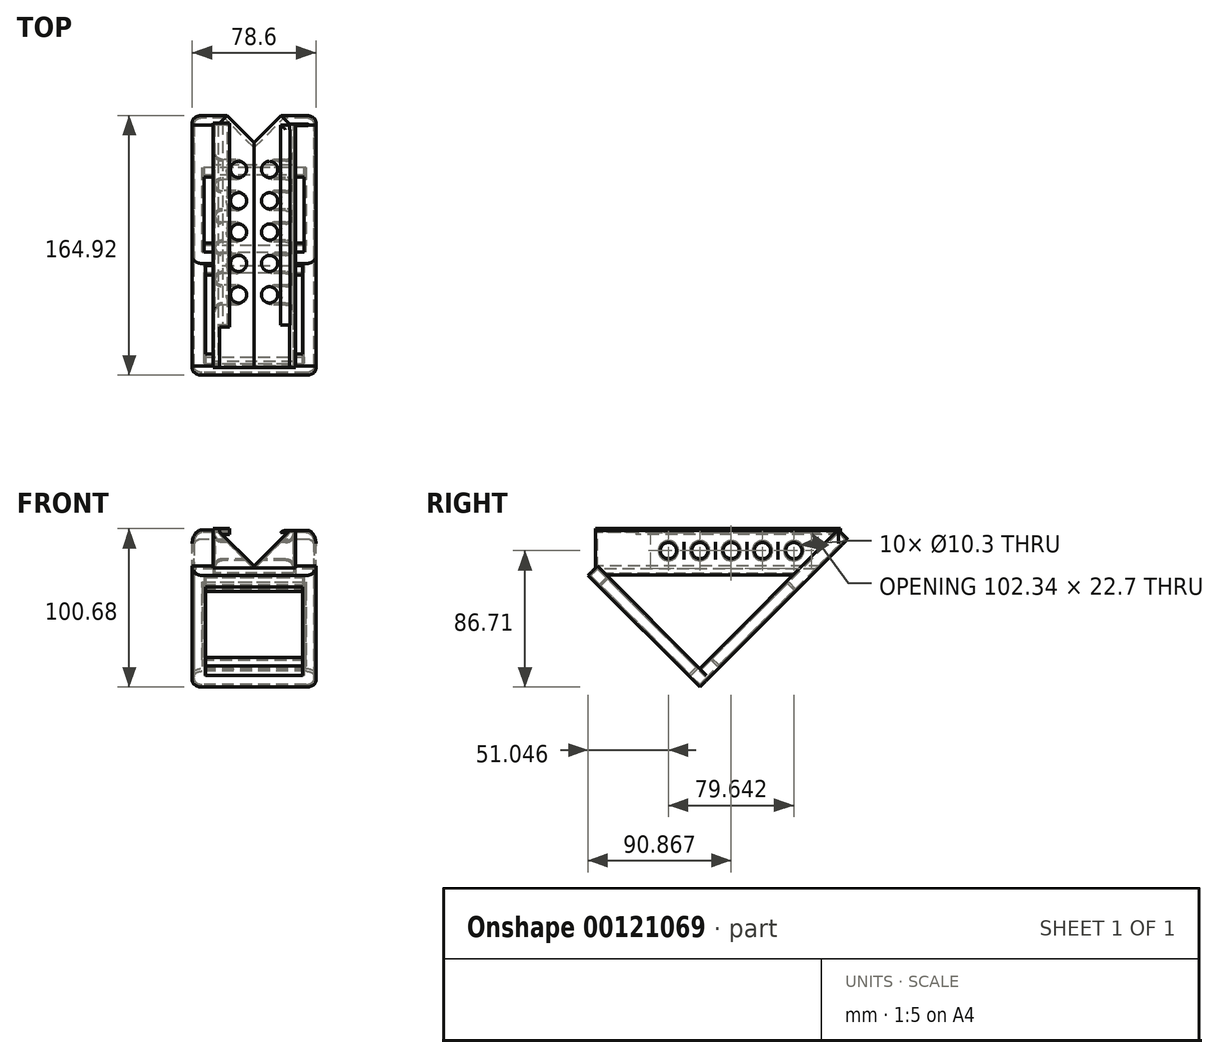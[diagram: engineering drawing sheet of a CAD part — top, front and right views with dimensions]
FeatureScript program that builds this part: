
annotation { "Feature Type Name" : "Feature", "Feature Type Description" : "" }
export const myFeature = defineFeature(function(context is Context, id is Id, definition is map)
    precondition{}
    {
        {
            var Q0;
            Q0=qCreatedBy(makeId("Front.planeOp"),FACE);
            var sketch = newSketch(context, id + "F0", { "sketchPlane" : qUnion([Q0])});
            skLineSegment(sketch, "E0", {"start": v(0, 0) * mm, "end": v(0, 23) * mm, "construction": true});
            skLineSegment(sketch, "E1", {"start": v(0, 0) * mm, "end": v(23, 23) * mm});
            skLineSegment(sketch, "E2", {"start": v(0, 0) * mm, "end": v(-23, 23) * mm});
            skLineSegment(sketch, "E3", {"start": v(-23, 23) * mm, "end": v(23, 23) * mm});
            skSolve(sketch);
        }
        {
            var Q0;
            Q0=qCreatedBy(makeId("Right.planeOp"),FACE);
            var sketch = newSketch(context, id + "F1", { "sketchPlane" : qUnion([Q0])});
            skPoint(sketch, "E4.0", {"position": v(0, 23) * mm});
            skLineSegment(sketch, "E5.0", {"start": v(0, 0) * mm, "end": v(0, 23) * mm, "construction": true});
            skLineSegment(sketch, "E6", {"start": v(-88.02, 23) * mm, "end": v(88.02, 23) * mm});
            skLineSegment(sketch, "E7", {"start": v(88.02, 23) * mm, "end": v(0, -65.02) * mm});
            skLineSegment(sketch, "E8", {"start": v(-65.02, 0) * mm, "end": v(65.02, 0) * mm, "construction": true});
            skLineSegment(sketch, "E9", {"start": v(-88.02, 23) * mm, "end": v(0, -65.02) * mm});
            skLineSegment(sketch, "E10", {"start": v(-88.02, 23) * mm, "end": v(-92.27, 18.76) * mm});
            skLineSegment(sketch, "E11", {"start": v(-92.27, 18.76) * mm, "end": v(0, -73.5) * mm});
            skLineSegment(sketch, "E12", {"start": v(0, -73.5) * mm, "end": v(92.27, 18.76) * mm});
            skLineSegment(sketch, "E13", {"start": v(92.27, 18.76) * mm, "end": v(88.02, 23) * mm});
            skLineSegment(sketch, "E14", {"start": v(-62.42, -2.6) * mm, "end": v(62.42, -2.6) * mm});
            skLineSegment(sketch, "E15", {"start": v(-65.02, 0) * mm, "end": v(-69.27, -4.24) * mm});
            skLineSegment(sketch, "E16", {"start": v(-65.02, 0) * mm, "end": v(-65.02, 23) * mm});
            skSolve(sketch);
        }
        {
            var Q0;
            {var subQ8=sQuery(id+"F1.wireOp",EDGE,"E12");Q0=makeQuery(id+"F1.imprint","IMPRINT",FACE,{"disambiguationData":[TD([[makeQuery(id+"F1.imprint","IMPRINT",EDGE,{"derivedFrom":subQ8}),1.0]])]});}
            extrude(context, id + "F2", {"entities" : qUnion([Q0]), "endBound" : BoundingType.SYMMETRIC, "depth" : 76.2 * mm});
        }
        {
            var Q0;
            {var subQ0=sQuery(id+"F1.wireOp",EDGE,"E14");Q0=makeQuery(id+"F1.imprint","IMPRINT",FACE,{"disambiguationData":[TD([[makeQuery(id+"F1.imprint","IMPRINT",EDGE,{"derivedFrom":subQ0}),1.0]])]});}
            extrude(context, id + "F3", {"entities" : qUnion([Q0]), "endBound" : BoundingType.SYMMETRIC, "depth" : 50 * mm});
        }
        {
            var Q0;
            Q0 = qSketchRegion(id + "F0", true);
            extrude(context, id + "F4", {"entities" : qUnion([Q0]), "operationType" : NewBodyOperationType.REMOVE, "endBound" : BoundingType.SYMMETRIC, "oppositeDirection" : true, "depth" : 200 * mm});
        }
        {
            var Q0;
            Q0=qCreatedBy(makeId("Top.planeOp"),FACE);
            var sketch = newSketch(context, id + "F5", { "sketchPlane" : qUnion([Q0])});
            skLineSegment(sketch, "E17.0", {"start": v(-22, 92.27) * mm, "end": v(-22, -62.42) * mm});
            skLineSegment(sketch, "E18.0", {"start": v(22, 92.27) * mm, "end": v(22, -62.42) * mm});
            skLineSegment(sketch, "E19", {"start": v(-22, -39.18) * mm, "end": v(-11.84, -39.18) * mm});
            skLineSegment(sketch, "E20", {"start": v(-11.84, -39.18) * mm, "end": v(-22, -50.42) * mm});
            skLineSegment(sketch, "E21", {"start": v(-22, -39.18) * mm, "end": v(22, -39.18) * mm, "construction": true});
            skPoint(sketch, "E22", {"position": v(0, -39.18) * mm});
            skLineSegment(sketch, "E23", {"start": v(22, -39.18) * mm, "end": v(11.84, -39.18) * mm});
            skLineSegment(sketch, "E24", {"start": v(11.84, -39.18) * mm, "end": v(22, -50.42) * mm});
            skPoint(sketch, "E25.0", {"position": v(0, 92.27) * mm});
            skLineSegment(sketch, "E26", {"start": v(-22, 92.27) * mm, "end": v(22, 92.27) * mm, "construction": true});
            skLineSegment(sketch, "E27.0", {"start": v(0, -65.02) * mm, "end": v(0, 65.02) * mm});
            skLineSegment(sketch, "E28.0", {"start": v(25, -62.42) * mm, "end": v(-25, -62.42) * mm});
            skSolve(sketch);
        }
        {
            var Q0;
            Q0=makeQuery(id+"F2.opExtrude","SWEPT_FACE",FACE,{"disambiguationData":[OSD([sQuery(id+"F1.wireOp",EDGE,"E12")])]});
            var sketch = newSketch(context, id + "F6", { "sketchPlane" : qUnion([Q0])});
            skLineSegment(sketch, "E29.bottom", {"start": v(38.1, -51.98) * mm, "end": v(22.56, -51.98) * mm, "construction": true});
            skLineSegment(sketch, "E29.top", {"start": v(38.1, -36.43) * mm, "end": v(22.56, -36.43) * mm});
            skLineSegment(sketch, "E29.left", {"start": v(38.1, -51.98) * mm, "end": v(38.1, -36.43) * mm});
            skLineSegment(sketch, "E29.right", {"start": v(22.56, -51.98) * mm, "end": v(22.56, -36.43) * mm});
            skLineSegment(sketch, "E30.bottom", {"start": v(-38.1, -51.98) * mm, "end": v(-22.55, -51.98) * mm, "construction": true});
            skLineSegment(sketch, "E30.top", {"start": v(-38.1, -36.43) * mm, "end": v(-22.55, -36.43) * mm});
            skLineSegment(sketch, "E30.left", {"start": v(-38.1, -51.98) * mm, "end": v(-38.1, -36.43) * mm, "construction": true});
            skLineSegment(sketch, "E30.right", {"start": v(-22.55, -51.98) * mm, "end": v(-22.55, -36.43) * mm});
            skLineSegment(sketch, "E31.bottom", {"start": v(22.56, 78.5) * mm, "end": v(38.1, 78.5) * mm, "construction": true});
            skLineSegment(sketch, "E31.top", {"start": v(22.56, 62.96) * mm, "end": v(38.1, 62.96) * mm});
            skLineSegment(sketch, "E31.left", {"start": v(22.56, 78.5) * mm, "end": v(22.56, 62.96) * mm});
            skLineSegment(sketch, "E31.right", {"start": v(38.1, 78.5) * mm, "end": v(38.1, 62.96) * mm, "construction": true});
            skCircle(sketch, "E32", {"center": v(-30.32, -44.2) * mm, "radius": 7 * mm});
            skCircle(sketch, "E33", {"center": v(30.33, -44.2) * mm, "radius": 7 * mm});
            skPoint(sketch, "E33.centerSnap0", {"position": v(30.33, -51.98) * mm});
            skCircle(sketch, "E34", {"center": v(30.33, 70.73) * mm, "radius": 7 * mm});
            skLineSegment(sketch, "E35", {"start": v(-30.32, -51.98) * mm, "end": v(-30.32, -36.43) * mm, "construction": true});
            skLineSegment(sketch, "E36", {"start": v(30.33, -51.98) * mm, "end": v(30.33, -36.43) * mm, "construction": true});
            skLineSegment(sketch, "E37", {"start": v(30.33, 78.5) * mm, "end": v(30.33, 62.96) * mm, "construction": true});
            skLineSegment(sketch, "E38.0.0", {"start": v(18.76, 78.5) * mm, "end": v(0, 51.98) * mm});
            skLineSegment(sketch, "E38.0.1", {"start": v(0, 51.98) * mm, "end": v(-18.76, 78.5) * mm});
            skLineSegment(sketch, "E38.0.2", {"start": v(-18.76, 78.5) * mm, "end": v(-38.1, 78.5) * mm});
            skLineSegment(sketch, "E38.0.3", {"start": v(-38.1, 78.5) * mm, "end": v(-38.1, -51.98) * mm});
            skLineSegment(sketch, "E38.0.4", {"start": v(-38.1, -51.98) * mm, "end": v(38.1, -51.98) * mm});
            skLineSegment(sketch, "E38.0.5", {"start": v(38.1, -51.98) * mm, "end": v(38.1, 78.5) * mm});
            skLineSegment(sketch, "E38.0.6", {"start": v(38.1, 78.5) * mm, "end": v(18.76, 78.5) * mm});
            skPoint(sketch, "E39.0", {"position": v(0, 78.5) * mm});
            skLineSegment(sketch, "E40.bottom", {"start": v(-38.1, 78.5) * mm, "end": v(-22.56, 78.5) * mm, "construction": true});
            skLineSegment(sketch, "E40.top", {"start": v(-38.1, 62.96) * mm, "end": v(-22.56, 62.96) * mm});
            skLineSegment(sketch, "E40.left", {"start": v(-38.1, 78.5) * mm, "end": v(-38.1, 62.96) * mm, "construction": true});
            skLineSegment(sketch, "E40.right", {"start": v(-22.56, 78.5) * mm, "end": v(-22.56, 62.96) * mm});
            skCircle(sketch, "E41", {"center": v(-30.33, 70.73) * mm, "radius": 7 * mm});
            skLineSegment(sketch, "E42", {"start": v(-30.33, 78.5) * mm, "end": v(-30.33, 62.96) * mm, "construction": true});
            skSolve(sketch);
        }
        {
            var Q0;
            {var subQ2=sQuery(id+"F1.wireOp",EDGE,"E6");Q0=makeQuery(id+"F4.boolean.opBoolean","SPLIT",FACE,{"disambiguationData":[TD([makeQuery(id+"F4.opExtrude","SWEPT_FACE",FACE,{"disambiguationData":[OSD([sQuery(id+"F0.wireOp",EDGE,"E1")])]})])],"derivedFrom":makeQuery(id+"F3.opExtrude","SWEPT_FACE",FACE,{"disambiguationData":[OSD([subQ2])]})});}
            var sketch = newSketch(context, id + "F7", { "sketchPlane" : qUnion([Q0])});
            skLineSegment(sketch, "E43.0.0", {"start": v(22, -50.42) * mm, "end": v(22, -39.18) * mm});
            skLineSegment(sketch, "E43.0.1", {"start": v(22, -39.18) * mm, "end": v(11.84, -39.18) * mm});
            skLineSegment(sketch, "E43.0.2", {"start": v(11.84, -39.18) * mm, "end": v(22, -50.42) * mm});
            skLineSegment(sketch, "E44.0.0", {"start": v(-11.84, -39.18) * mm, "end": v(-22, -39.18) * mm});
            skLineSegment(sketch, "E44.0.1", {"start": v(-22, -39.18) * mm, "end": v(-22, -50.42) * mm});
            skLineSegment(sketch, "E44.0.2", {"start": v(-22, -50.42) * mm, "end": v(-11.84, -39.18) * mm});
            skLineSegment(sketch, "E45.0.5", {"start": v(25, -39.18) * mm, "end": v(25, 88.02) * mm});
            skLineSegment(sketch, "E46.0.2", {"start": v(-25, 88.02) * mm, "end": v(-25, -39.18) * mm});
            skLineSegment(sketch, "E47.bottom", {"start": v(25, -39.18) * mm, "end": v(16.92, -39.18) * mm});
            skLineSegment(sketch, "E47.top", {"start": v(25, 88.02) * mm, "end": v(16.92, 88.02) * mm});
            skLineSegment(sketch, "E47.right", {"start": v(16.92, -39.18) * mm, "end": v(16.92, 88.02) * mm});
            skPoint(sketch, "E48.oppositeSnap0", {"position": v(-16.92, -39.18) * mm});
            skLineSegment(sketch, "E48.bottom", {"start": v(-25, -39.18) * mm, "end": v(-16.92, -39.18) * mm});
            skLineSegment(sketch, "E48.top", {"start": v(-25, 88.02) * mm, "end": v(-16.92, 88.02) * mm});
            skLineSegment(sketch, "E48.left", {"start": v(-25, -39.18) * mm, "end": v(-25, 88.02) * mm});
            skLineSegment(sketch, "E48.right", {"start": v(-16.92, -39.18) * mm, "end": v(-16.92, 88.02) * mm});
            skPoint(sketch, "E49.0", {"position": v(0, 65.02) * mm});
            skPoint(sketch, "E50.0", {"position": v(-25, 88.02) * mm});
            skPoint(sketch, "E51.0", {"position": v(25, 88.02) * mm});
            skSolve(sketch);
        }
        {
            var Q0;
            Q0=qCreatedBy(makeId("Right.planeOp"),FACE);
            var sketch = newSketch(context, id + "F8", { "sketchPlane" : qUnion([Q0])});
            skLineSegment(sketch, "E52.0.1", {"start": v(0, 0) * mm, "end": v(0, 23) * mm, "construction": true});
            skLineSegment(sketch, "E52.0.2", {"start": v(0, 23) * mm, "end": v(-88.02, 23) * mm});
            skLineSegment(sketch, "E53.0.3", {"start": v(88.02, 23) * mm, "end": v(0, 23) * mm});
            skPoint(sketch, "E54.0", {"position": v(0, 23) * mm});
            skLineSegment(sketch, "E55", {"start": v(19.91, 0) * mm, "end": v(19.91, 23) * mm, "construction": true});
            skLineSegment(sketch, "E56", {"start": v(39.81, 0) * mm, "end": v(39.81, 23) * mm, "construction": true});
            skPoint(sketch, "E57", {"position": v(0, 11.5) * mm});
            skPoint(sketch, "E58", {"position": v(19.91, 11.5) * mm});
            skPoint(sketch, "E59", {"position": v(39.81, 11.5) * mm});
            skCircle(sketch, "E60", {"center": v(0, 11.5) * mm, "radius": 6.35 * mm});
            skCircle(sketch, "E61", {"center": v(19.91, 11.5) * mm, "radius": 6.35 * mm});
            skCircle(sketch, "E62", {"center": v(39.81, 11.5) * mm, "radius": 6.35 * mm});
            skLineSegment(sketch, "E63", {"start": v(-19.91, 0) * mm, "end": v(-19.91, 23) * mm, "construction": true});
            skPoint(sketch, "E64", {"position": v(-19.91, 11.5) * mm});
            skCircle(sketch, "E65", {"center": v(-19.91, 11.5) * mm, "radius": 6.35 * mm});
            skLineSegment(sketch, "E66", {"start": v(59.73, 0) * mm, "end": v(59.73, 23) * mm, "construction": true});
            skPoint(sketch, "E67", {"position": v(59.73, 11.5) * mm});
            skCircle(sketch, "E68", {"center": v(59.73, 11.5) * mm, "radius": 6.35 * mm});
            skPoint(sketch, "E69.0", {"position": v(-88.02, 23) * mm});
            skPoint(sketch, "E70.0", {"position": v(88.02, 23) * mm});
            skLineSegment(sketch, "E71.0", {"start": v(-65.02, 0) * mm, "end": v(65.02, 0) * mm});
            skSolve(sketch);
        }
        {
            var Q0;
            Q0=makeQuery(id+"F8.imprint","IMPRINT",FACE,{"disambiguationData":[TD([[makeQuery(id+"F8.imprint","IMPRINT",EDGE,{"derivedFrom":sQuery(id+"F8.wireOp",EDGE,"E65")}),1.0]])]});
            var Q1;
            Q1=makeQuery(id+"F8.imprint","IMPRINT",FACE,{"disambiguationData":[TD([[makeQuery(id+"F8.imprint","IMPRINT",EDGE,{"derivedFrom":sQuery(id+"F8.wireOp",EDGE,"E60")}),1.0]])]});
            var Q2;
            Q2=makeQuery(id+"F8.imprint","IMPRINT",FACE,{"disambiguationData":[TD([[makeQuery(id+"F8.imprint","IMPRINT",EDGE,{"derivedFrom":sQuery(id+"F8.wireOp",EDGE,"E61")}),1.0]])]});
            var Q3;
            Q3=makeQuery(id+"F8.imprint","IMPRINT",FACE,{"disambiguationData":[TD([[makeQuery(id+"F8.imprint","IMPRINT",EDGE,{"derivedFrom":sQuery(id+"F8.wireOp",EDGE,"E62")}),1.0]])]});
            var Q4;
            Q4=makeQuery(id+"F8.imprint","IMPRINT",FACE,{"disambiguationData":[TD([[makeQuery(id+"F8.imprint","IMPRINT",EDGE,{"derivedFrom":sQuery(id+"F8.wireOp",EDGE,"E68")}),1.0]])]});
            extrude(context, id + "F9", {"entities" : qUnion([Q0, Q1, Q2, Q3, Q4]), "operationType" : NewBodyOperationType.REMOVE, "endBound" : BoundingType.SYMMETRIC, "depth" : 177.8 * mm});
        }
        {
            var Q0;
            {var subQ4=sQuery(id+"F7.wireOp",EDGE,"E45.0.5");Q0=makeQuery(id+"F7.imprint","IMPRINT",FACE,{"disambiguationData":[TD([[makeQuery(id+"F7.imprint","IMPRINT",EDGE,{"derivedFrom":subQ4}),1.0]])]});}
            var Q1;
            {var subQ3=sQuery(id+"F7.wireOp",EDGE,"E47.right");Q1=makeQuery(id+"F7.imprint","IMPRINT",FACE,{"disambiguationData":[TD([[makeQuery(id+"F7.imprint","IMPRINT",EDGE,{"derivedFrom":subQ3}),-1.0]])]});}
            var Q2;
            Q2=makeQuery(id+"F7.imprint","IMPRINT",FACE,{"disambiguationData":[TD([[makeQuery(id+"F7.imprint","IMPRINT",EDGE,{"derivedFrom":sQuery(id+"F7.wireOp",EDGE,"E48.top")}),-1.0]])]});
            var Q3;
            {var subQ0=sQuery(id+"F7.wireOp",EDGE,"E43.0.0");Q3=makeQuery(id+"F7.imprint","IMPRINT",FACE,{"disambiguationData":[TD([[makeQuery(id+"F7.imprint","IMPRINT",EDGE,{"derivedFrom":subQ0}),-1.0]])]});}
            var Q4;
            {var subQ2=sQuery(id+"F1.wireOp",EDGE,"E6");Q4=makeQuery(id+"F4.boolean.opBoolean","SPLIT",FACE,{"disambiguationData":[TD([makeQuery(id+"F4.opExtrude","SWEPT_FACE",FACE,{"disambiguationData":[OSD([sQuery(id+"F0.wireOp",EDGE,"E2")])]})])],"derivedFrom":makeQuery(id+"F3.opExtrude","SWEPT_FACE",FACE,{"disambiguationData":[OSD([subQ2])]})});}
            extrude(context, id + "F10", {"entities" : qUnion([Q0, Q1, Q2, Q3, Q4]), "operationType" : NewBodyOperationType.ADD, "depth" : 1.27 * mm});
        }
        {
            var Q0;
            {var subQ0=sQuery(id+"F6.wireOp",EDGE,"E38.0.4");Q0=makeQuery(id+"FcCoG44jGWUjaJj_4.boolean.opBoolean","MERGE",FACE,{"derivedFrom":[makeQuery(id+"F2.opExtrude","SWEPT_FACE",FACE,{"disambiguationData":[OSD([sQuery(id+"F1.wireOp",EDGE,"E11")])]}),makeQuery(id+"FcCoG44jGWUjaJj_4.opExtrude","SWEPT_FACE",FACE,{"disambiguationData":[OSD([subQ0]),TDD([makeQuery(id+"F6.imprint","IMPRINT",EDGE,{"disambiguationData":[TD([[makeQuery(id+"F6.imprint","INTERSECT",VERTEX,{"derivedFrom":[sQuery(id+"F6.wireOp",EDGE,"E38.0.3"),subQ0]}),-1.0]])],"derivedFrom":subQ0})])]}),makeQuery(id+"FcCoG44jGWUjaJj_4.opExtrude","SWEPT_FACE",FACE,{"disambiguationData":[OSD([subQ0]),TDD([makeQuery(id+"F6.imprint","IMPRINT",EDGE,{"disambiguationData":[TD([[makeQuery(id+"F6.imprint","INTERSECT",VERTEX,{"derivedFrom":[subQ0,sQuery(id+"F6.wireOp",EDGE,"E38.0.5")]}),1.0]])],"derivedFrom":subQ0})])]})]});}
            var sketch = newSketch(context, id + "F11", { "sketchPlane" : qUnion([Q0])});
            skLineSegment(sketch, "E72.bottom", {"start": v(-31.85, 37.98) * mm, "end": v(31.85, 37.98) * mm});
            skLineSegment(sketch, "E72.top", {"start": v(-31.85, -43.88) * mm, "end": v(31.85, -43.88) * mm});
            skLineSegment(sketch, "E72.left", {"start": v(-31.85, 37.98) * mm, "end": v(-31.85, -43.88) * mm});
            skLineSegment(sketch, "E72.right", {"start": v(31.85, 37.98) * mm, "end": v(31.85, -43.88) * mm});
            skPoint(sketch, "E73.0", {"position": v(-38.1, 45.98) * mm});
            skPoint(sketch, "E74.0", {"position": v(38.1, -45.98) * mm});
            skLineSegment(sketch, "E75.0", {"start": v(22.55, -51.98) * mm, "end": v(-22.56, -51.98) * mm});
            skPoint(sketch, "E76.0", {"position": v(0, 45.98) * mm});
            skSolve(sketch);
        }
        {
            var Q0;
            Q0=makeQuery(id+"F11.imprint","IMPRINT",FACE,{"disambiguationData":[TD([[makeQuery(id+"F11.imprint","IMPRINT",EDGE,{"derivedFrom":sQuery(id+"F11.wireOp",EDGE,"E72.bottom")}),-1.0]])]});
            var Q1;
            Q1=makeQuery(id+"F2.opExtrude","SWEPT_FACE",FACE,{"disambiguationData":[OSD([sQuery(id+"F1.wireOp",EDGE,"E9")])]});
            extrude(context, id + "F12", {"entities" : qUnion([Q0]), "operationType" : NewBodyOperationType.REMOVE, "endBound" : BoundingType.UP_TO_SURFACE, "oppositeDirection" : true, "endBoundEntityFace" : qUnion([Q1]), "depth" : 25.4 * mm});
        }
        {
            var Q0;
            Q0=makeQuery(id+"FcCoG44jGWUjaJj_4.opExtrude","SWEPT_EDGE",EDGE,{"disambiguationData":[OSD([sQuery(id+"F6.wireOp",EDGE,"E31.top"),sQuery(id+"F6.wireOp",EDGE,"E38.0.5")])]});
            var Q1;
            Q1=makeQuery(id+"F2.opExtrude","CAP_EDGE",EDGE,{"disambiguationData":[OSD([sQuery(id+"F1.wireOp",EDGE,"E7")])],"isStart":true});
            var Q2;
            Q2=makeQuery(id+"F2.opExtrude","CAP_EDGE",EDGE,{"disambiguationData":[OSD([sQuery(id+"F1.wireOp",EDGE,"E7")])],"isStart":false});
            var Q3;
            Q3=makeQuery(id+"FcCoG44jGWUjaJj_4.boolean.opBoolean","MERGE",EDGE,{"derivedFrom":[makeQuery(id+"F2.opExtrude","CAP_EDGE",EDGE,{"disambiguationData":[OSD([sQuery(id+"F1.wireOp",EDGE,"E11")])],"isStart":false}),makeQuery(id+"FcCoG44jGWUjaJj_4.opExtrude","SWEPT_EDGE",EDGE,{"disambiguationData":[OSD([sQuery(id+"F6.wireOp",EDGE,"E38.0.3"),sQuery(id+"F6.wireOp",EDGE,"E38.0.4")])]})]});
            var Q4;
            Q4=makeQuery(id+"FcCoG44jGWUjaJj_4.boolean.opBoolean","MERGE",EDGE,{"derivedFrom":[makeQuery(id+"F2.opExtrude","CAP_EDGE",EDGE,{"disambiguationData":[OSD([sQuery(id+"F1.wireOp",EDGE,"E11")])],"isStart":true}),makeQuery(id+"FcCoG44jGWUjaJj_4.opExtrude","SWEPT_EDGE",EDGE,{"disambiguationData":[OSD([sQuery(id+"F6.wireOp",EDGE,"E38.0.4"),sQuery(id+"F6.wireOp",EDGE,"E38.0.5")])]})]});
            var Q5;
            Q5=makeQuery(id+"FcCoG44jGWUjaJj_4.opExtrude","SWEPT_EDGE",EDGE,{"disambiguationData":[OSD([sQuery(id+"F6.wireOp",EDGE,"E29.right"),sQuery(id+"F6.wireOp",EDGE,"E38.0.4")])]});
            var Q6;
            Q6=makeQuery(id+"FcCoG44jGWUjaJj_4.opExtrude","SWEPT_EDGE",EDGE,{"disambiguationData":[OSD([sQuery(id+"F6.wireOp",EDGE,"E30.right"),sQuery(id+"F6.wireOp",EDGE,"E38.0.4")])]});
            var Q7;
            Q7=makeQuery(id+"FcCoG44jGWUjaJj_4.opExtrude","SWEPT_EDGE",EDGE,{"disambiguationData":[OSD([sQuery(id+"F6.wireOp",EDGE,"E30.top"),sQuery(id+"F6.wireOp",EDGE,"E30.right")])]});
            var Q8;
            Q8=makeQuery(id+"FcCoG44jGWUjaJj_4.opExtrude","SWEPT_EDGE",EDGE,{"disambiguationData":[OSD([sQuery(id+"F6.wireOp",EDGE,"E30.top"),sQuery(id+"F6.wireOp",EDGE,"E38.0.3")])]});
            var Q9;
            Q9=makeQuery(id+"FcCoG44jGWUjaJj_4.opExtrude","SWEPT_EDGE",EDGE,{"disambiguationData":[OSD([sQuery(id+"F6.wireOp",EDGE,"E38.0.3"),sQuery(id+"F6.wireOp",EDGE,"E40.top")])]});
            var Q10;
            Q10=makeQuery(id+"FcCoG44jGWUjaJj_4.opExtrude","SWEPT_EDGE",EDGE,{"disambiguationData":[OSD([sQuery(id+"F6.wireOp",EDGE,"E40.top"),sQuery(id+"F6.wireOp",EDGE,"E40.right")])]});
            var Q11;
            Q11=makeQuery(id+"FcCoG44jGWUjaJj_4.boolean.opBoolean","MERGE",EDGE,{"derivedFrom":[makeQuery(id+"F2.opExtrude","CAP_EDGE",EDGE,{"disambiguationData":[OSD([sQuery(id+"F1.wireOp",EDGE,"E13")])],"isStart":false}),makeQuery(id+"FcCoG44jGWUjaJj_4.opExtrude","SWEPT_EDGE",EDGE,{"disambiguationData":[OSD([sQuery(id+"F6.wireOp",EDGE,"E38.0.2"),sQuery(id+"F6.wireOp",EDGE,"E38.0.3")])]})]});
            var Q12;
            Q12=makeQuery(id+"FcCoG44jGWUjaJj_4.opExtrude","SWEPT_EDGE",EDGE,{"disambiguationData":[OSD([sQuery(id+"F6.wireOp",EDGE,"E38.0.2"),sQuery(id+"F6.wireOp",EDGE,"E40.right")])]});
            var Q13;
            Q13=makeQuery(id+"FcCoG44jGWUjaJj_4.opExtrude","SWEPT_EDGE",EDGE,{"disambiguationData":[OSD([sQuery(id+"F6.wireOp",EDGE,"E31.left"),sQuery(id+"F6.wireOp",EDGE,"E38.0.6")])]});
            var Q14;
            Q14=makeQuery(id+"FcCoG44jGWUjaJj_4.boolean.opBoolean","MERGE",EDGE,{"derivedFrom":[makeQuery(id+"F2.opExtrude","CAP_EDGE",EDGE,{"disambiguationData":[OSD([sQuery(id+"F1.wireOp",EDGE,"E13")])],"isStart":true}),makeQuery(id+"FcCoG44jGWUjaJj_4.opExtrude","SWEPT_EDGE",EDGE,{"disambiguationData":[OSD([sQuery(id+"F6.wireOp",EDGE,"E38.0.5"),sQuery(id+"F6.wireOp",EDGE,"E38.0.6")])]})]});
            var Q15;
            Q15=makeQuery(id+"FcCoG44jGWUjaJj_4.opExtrude","SWEPT_EDGE",EDGE,{"disambiguationData":[OSD([sQuery(id+"F6.wireOp",EDGE,"E31.top"),sQuery(id+"F6.wireOp",EDGE,"E31.left")])]});
            var Q16;
            Q16=makeQuery(id+"FcCoG44jGWUjaJj_4.opExtrude","SWEPT_EDGE",EDGE,{"disambiguationData":[OSD([sQuery(id+"F6.wireOp",EDGE,"E29.top"),sQuery(id+"F6.wireOp",EDGE,"E29.right")])]});
            var Q17;
            Q17=makeQuery(id+"FcCoG44jGWUjaJj_4.opExtrude","SWEPT_EDGE",EDGE,{"disambiguationData":[OSD([sQuery(id+"F6.wireOp",EDGE,"E29.top"),sQuery(id+"F6.wireOp",EDGE,"E38.0.5")])]});
            var Q18;
            Q18=makeQuery(id+"F9.boolean.opBoolean","INTERSECT",EDGE,{"derivedFrom":[makeQuery(id+"F3.opExtrude","CAP_FACE",FACE,{"disambiguationData":[OSD([sQuery(id+"F1.wireOp",EDGE,"E6"),sQuery(id+"F1.wireOp",EDGE,"E7"),sQuery(id+"F1.wireOp",EDGE,"E9"),sQuery(id+"F1.wireOp",EDGE,"E14"),sQuery(id+"F1.wireOp",EDGE,"E16")])],"isStart":false}),makeQuery(id+"F9.opExtrude","SWEPT_FACE",FACE,{"disambiguationData":[OSD([sQuery(id+"F8.wireOp",EDGE,"E65")])]})]});
            var Q19;
            Q19=makeQuery(id+"F9.boolean.opBoolean","INTERSECT",EDGE,{"derivedFrom":[makeQuery(id+"F3.opExtrude","CAP_FACE",FACE,{"disambiguationData":[OSD([sQuery(id+"F1.wireOp",EDGE,"E6"),sQuery(id+"F1.wireOp",EDGE,"E7"),sQuery(id+"F1.wireOp",EDGE,"E9"),sQuery(id+"F1.wireOp",EDGE,"E14"),sQuery(id+"F1.wireOp",EDGE,"E16")])],"isStart":false}),makeQuery(id+"F9.opExtrude","SWEPT_FACE",FACE,{"disambiguationData":[OSD([sQuery(id+"F8.wireOp",EDGE,"E60")])]})]});
            var Q20;
            Q20=makeQuery(id+"F9.boolean.opBoolean","INTERSECT",EDGE,{"derivedFrom":[makeQuery(id+"F3.opExtrude","CAP_FACE",FACE,{"disambiguationData":[OSD([sQuery(id+"F1.wireOp",EDGE,"E6"),sQuery(id+"F1.wireOp",EDGE,"E7"),sQuery(id+"F1.wireOp",EDGE,"E9"),sQuery(id+"F1.wireOp",EDGE,"E14"),sQuery(id+"F1.wireOp",EDGE,"E16")])],"isStart":false}),makeQuery(id+"F9.opExtrude","SWEPT_FACE",FACE,{"disambiguationData":[OSD([sQuery(id+"F8.wireOp",EDGE,"E61")])]})]});
            var Q21;
            Q21=makeQuery(id+"F9.boolean.opBoolean","INTERSECT",EDGE,{"derivedFrom":[makeQuery(id+"F3.opExtrude","CAP_FACE",FACE,{"disambiguationData":[OSD([sQuery(id+"F1.wireOp",EDGE,"E6"),sQuery(id+"F1.wireOp",EDGE,"E7"),sQuery(id+"F1.wireOp",EDGE,"E9"),sQuery(id+"F1.wireOp",EDGE,"E14"),sQuery(id+"F1.wireOp",EDGE,"E16")])],"isStart":false}),makeQuery(id+"F9.opExtrude","SWEPT_FACE",FACE,{"disambiguationData":[OSD([sQuery(id+"F8.wireOp",EDGE,"E62")])]})]});
            var Q22;
            Q22=makeQuery(id+"F9.boolean.opBoolean","INTERSECT",EDGE,{"derivedFrom":[makeQuery(id+"F3.opExtrude","CAP_FACE",FACE,{"disambiguationData":[OSD([sQuery(id+"F1.wireOp",EDGE,"E6"),sQuery(id+"F1.wireOp",EDGE,"E7"),sQuery(id+"F1.wireOp",EDGE,"E9"),sQuery(id+"F1.wireOp",EDGE,"E14"),sQuery(id+"F1.wireOp",EDGE,"E16")])],"isStart":false}),makeQuery(id+"F9.opExtrude","SWEPT_FACE",FACE,{"disambiguationData":[OSD([sQuery(id+"F8.wireOp",EDGE,"E68")])]})]});
            var Q23;
            Q23=makeQuery(id+"F9.boolean.opBoolean","INTERSECT",EDGE,{"derivedFrom":[makeQuery(id+"F3.opExtrude","CAP_FACE",FACE,{"disambiguationData":[OSD([sQuery(id+"F1.wireOp",EDGE,"E6"),sQuery(id+"F1.wireOp",EDGE,"E7"),sQuery(id+"F1.wireOp",EDGE,"E9"),sQuery(id+"F1.wireOp",EDGE,"E14"),sQuery(id+"F1.wireOp",EDGE,"E16")])],"isStart":true}),makeQuery(id+"F9.opExtrude","SWEPT_FACE",FACE,{"disambiguationData":[OSD([sQuery(id+"F8.wireOp",EDGE,"E65")])]})]});
            var Q24;
            Q24=makeQuery(id+"F9.boolean.opBoolean","INTERSECT",EDGE,{"derivedFrom":[makeQuery(id+"F3.opExtrude","CAP_FACE",FACE,{"disambiguationData":[OSD([sQuery(id+"F1.wireOp",EDGE,"E6"),sQuery(id+"F1.wireOp",EDGE,"E7"),sQuery(id+"F1.wireOp",EDGE,"E9"),sQuery(id+"F1.wireOp",EDGE,"E14"),sQuery(id+"F1.wireOp",EDGE,"E16")])],"isStart":true}),makeQuery(id+"F9.opExtrude","SWEPT_FACE",FACE,{"disambiguationData":[OSD([sQuery(id+"F8.wireOp",EDGE,"E60")])]})]});
            var Q25;
            Q25=makeQuery(id+"F9.boolean.opBoolean","INTERSECT",EDGE,{"derivedFrom":[makeQuery(id+"F3.opExtrude","CAP_FACE",FACE,{"disambiguationData":[OSD([sQuery(id+"F1.wireOp",EDGE,"E6"),sQuery(id+"F1.wireOp",EDGE,"E7"),sQuery(id+"F1.wireOp",EDGE,"E9"),sQuery(id+"F1.wireOp",EDGE,"E14"),sQuery(id+"F1.wireOp",EDGE,"E16")])],"isStart":true}),makeQuery(id+"F9.opExtrude","SWEPT_FACE",FACE,{"disambiguationData":[OSD([sQuery(id+"F8.wireOp",EDGE,"E61")])]})]});
            var Q26;
            Q26=makeQuery(id+"F9.boolean.opBoolean","INTERSECT",EDGE,{"derivedFrom":[makeQuery(id+"F3.opExtrude","CAP_FACE",FACE,{"disambiguationData":[OSD([sQuery(id+"F1.wireOp",EDGE,"E6"),sQuery(id+"F1.wireOp",EDGE,"E7"),sQuery(id+"F1.wireOp",EDGE,"E9"),sQuery(id+"F1.wireOp",EDGE,"E14"),sQuery(id+"F1.wireOp",EDGE,"E16")])],"isStart":true}),makeQuery(id+"F9.opExtrude","SWEPT_FACE",FACE,{"disambiguationData":[OSD([sQuery(id+"F8.wireOp",EDGE,"E62")])]})]});
            var Q27;
            Q27=makeQuery(id+"F9.boolean.opBoolean","INTERSECT",EDGE,{"derivedFrom":[makeQuery(id+"F3.opExtrude","CAP_FACE",FACE,{"disambiguationData":[OSD([sQuery(id+"F1.wireOp",EDGE,"E6"),sQuery(id+"F1.wireOp",EDGE,"E7"),sQuery(id+"F1.wireOp",EDGE,"E9"),sQuery(id+"F1.wireOp",EDGE,"E14"),sQuery(id+"F1.wireOp",EDGE,"E16")])],"isStart":true}),makeQuery(id+"F9.opExtrude","SWEPT_FACE",FACE,{"disambiguationData":[OSD([sQuery(id+"F8.wireOp",EDGE,"E68")])]})]});
            fillet(context, id + "F13", {"entities" : qUnion([Q0, Q1, Q2, Q3, Q4, Q5, Q6, Q7, Q8, Q9, Q10, Q11, Q12, Q13, Q14, Q15, Q16, Q17, Q18, Q19, Q20, Q21, Q22, Q23, Q24, Q25, Q26, Q27]), "radius" : 5 * mm, "tangentPropagation" : true, "allowEdgeOverflow" : false});
        }
        {
            var Q0;
            Q0=makeQuery(id+"F10.opExtrude","CAP_EDGE",EDGE,{"disambiguationData":[OSD([sQuery(id+"F1.wireOp",EDGE,"E6")])],"isStart":false});
            var Q1;
            Q1=makeQuery(id+"F10.opExtrude","CAP_EDGE",EDGE,{"disambiguationData":[OSD([sQuery(id+"F1.wireOp",EDGE,"E6"),sQuery(id+"F7.wireOp",EDGE,"E45.0.5")])],"isStart":false});
            var Q2;
            Q2=makeQuery(id+"F3.opExtrude","CAP_EDGE",EDGE,{"disambiguationData":[OSD([sQuery(id+"F1.wireOp",EDGE,"E14")])],"isStart":false});
            var Q3;
            Q3=makeQuery(id+"F3.opExtrude","CAP_EDGE",EDGE,{"disambiguationData":[OSD([sQuery(id+"F1.wireOp",EDGE,"E14")])],"isStart":true});
            var Q4;
            Q4=makeQuery(id+"F9.boolean.opBoolean","INTERSECT",EDGE,{"derivedFrom":[makeQuery(id+"F3.opExtrude","CAP_FACE",FACE,{"disambiguationData":[OSD([sQuery(id+"F1.wireOp",EDGE,"E6"),sQuery(id+"F1.wireOp",EDGE,"E7"),sQuery(id+"F1.wireOp",EDGE,"E9"),sQuery(id+"F1.wireOp",EDGE,"E14")])],"isStart":false}),makeQuery(id+"F9.opExtrude","SWEPT_FACE",FACE,{"disambiguationData":[OSD([sQuery(id+"F8.wireOp",EDGE,"E65")])]})]});
            var Q5;
            Q5=makeQuery(id+"F9.boolean.opBoolean","INTERSECT",EDGE,{"derivedFrom":[makeQuery(id+"F3.opExtrude","CAP_FACE",FACE,{"disambiguationData":[OSD([sQuery(id+"F1.wireOp",EDGE,"E6"),sQuery(id+"F1.wireOp",EDGE,"E7"),sQuery(id+"F1.wireOp",EDGE,"E9"),sQuery(id+"F1.wireOp",EDGE,"E14")])],"isStart":false}),makeQuery(id+"F9.opExtrude","SWEPT_FACE",FACE,{"disambiguationData":[OSD([sQuery(id+"F8.wireOp",EDGE,"E60")])]})]});
            var Q6;
            Q6=makeQuery(id+"F9.boolean.opBoolean","INTERSECT",EDGE,{"derivedFrom":[makeQuery(id+"F3.opExtrude","CAP_FACE",FACE,{"disambiguationData":[OSD([sQuery(id+"F1.wireOp",EDGE,"E6"),sQuery(id+"F1.wireOp",EDGE,"E7"),sQuery(id+"F1.wireOp",EDGE,"E9"),sQuery(id+"F1.wireOp",EDGE,"E14")])],"isStart":false}),makeQuery(id+"F9.opExtrude","SWEPT_FACE",FACE,{"disambiguationData":[OSD([sQuery(id+"F8.wireOp",EDGE,"E61")])]})]});
            var Q7;
            Q7=makeQuery(id+"F9.boolean.opBoolean","INTERSECT",EDGE,{"derivedFrom":[makeQuery(id+"F3.opExtrude","CAP_FACE",FACE,{"disambiguationData":[OSD([sQuery(id+"F1.wireOp",EDGE,"E6"),sQuery(id+"F1.wireOp",EDGE,"E7"),sQuery(id+"F1.wireOp",EDGE,"E9"),sQuery(id+"F1.wireOp",EDGE,"E14")])],"isStart":false}),makeQuery(id+"F9.opExtrude","SWEPT_FACE",FACE,{"disambiguationData":[OSD([sQuery(id+"F8.wireOp",EDGE,"E62")])]})]});
            var Q8;
            Q8=makeQuery(id+"F9.boolean.opBoolean","INTERSECT",EDGE,{"derivedFrom":[makeQuery(id+"F3.opExtrude","CAP_FACE",FACE,{"disambiguationData":[OSD([sQuery(id+"F1.wireOp",EDGE,"E6"),sQuery(id+"F1.wireOp",EDGE,"E7"),sQuery(id+"F1.wireOp",EDGE,"E9"),sQuery(id+"F1.wireOp",EDGE,"E14")])],"isStart":false}),makeQuery(id+"F9.opExtrude","SWEPT_FACE",FACE,{"disambiguationData":[OSD([sQuery(id+"F8.wireOp",EDGE,"E68")])]})]});
            var Q9;
            Q9=makeQuery(id+"F9.boolean.opBoolean","INTERSECT",EDGE,{"derivedFrom":[makeQuery(id+"F3.opExtrude","CAP_FACE",FACE,{"disambiguationData":[OSD([sQuery(id+"F1.wireOp",EDGE,"E6"),sQuery(id+"F1.wireOp",EDGE,"E7"),sQuery(id+"F1.wireOp",EDGE,"E9"),sQuery(id+"F1.wireOp",EDGE,"E14")])],"isStart":true}),makeQuery(id+"F9.opExtrude","SWEPT_FACE",FACE,{"disambiguationData":[OSD([sQuery(id+"F8.wireOp",EDGE,"E65")])]})]});
            var Q10;
            Q10=makeQuery(id+"F9.boolean.opBoolean","INTERSECT",EDGE,{"derivedFrom":[makeQuery(id+"F3.opExtrude","CAP_FACE",FACE,{"disambiguationData":[OSD([sQuery(id+"F1.wireOp",EDGE,"E6"),sQuery(id+"F1.wireOp",EDGE,"E7"),sQuery(id+"F1.wireOp",EDGE,"E9"),sQuery(id+"F1.wireOp",EDGE,"E14")])],"isStart":true}),makeQuery(id+"F9.opExtrude","SWEPT_FACE",FACE,{"disambiguationData":[OSD([sQuery(id+"F8.wireOp",EDGE,"E60")])]})]});
            var Q11;
            Q11=makeQuery(id+"F9.boolean.opBoolean","INTERSECT",EDGE,{"derivedFrom":[makeQuery(id+"F3.opExtrude","CAP_FACE",FACE,{"disambiguationData":[OSD([sQuery(id+"F1.wireOp",EDGE,"E6"),sQuery(id+"F1.wireOp",EDGE,"E7"),sQuery(id+"F1.wireOp",EDGE,"E9"),sQuery(id+"F1.wireOp",EDGE,"E14")])],"isStart":true}),makeQuery(id+"F9.opExtrude","SWEPT_FACE",FACE,{"disambiguationData":[OSD([sQuery(id+"F8.wireOp",EDGE,"E61")])]})]});
            var Q12;
            Q12=makeQuery(id+"F9.boolean.opBoolean","INTERSECT",EDGE,{"derivedFrom":[makeQuery(id+"F3.opExtrude","CAP_FACE",FACE,{"disambiguationData":[OSD([sQuery(id+"F1.wireOp",EDGE,"E6"),sQuery(id+"F1.wireOp",EDGE,"E7"),sQuery(id+"F1.wireOp",EDGE,"E9"),sQuery(id+"F1.wireOp",EDGE,"E14")])],"isStart":true}),makeQuery(id+"F9.opExtrude","SWEPT_FACE",FACE,{"disambiguationData":[OSD([sQuery(id+"F8.wireOp",EDGE,"E62")])]})]});
            var Q13;
            Q13=makeQuery(id+"F9.boolean.opBoolean","INTERSECT",EDGE,{"derivedFrom":[makeQuery(id+"F3.opExtrude","CAP_FACE",FACE,{"disambiguationData":[OSD([sQuery(id+"F1.wireOp",EDGE,"E6"),sQuery(id+"F1.wireOp",EDGE,"E7"),sQuery(id+"F1.wireOp",EDGE,"E9"),sQuery(id+"F1.wireOp",EDGE,"E14")])],"isStart":true}),makeQuery(id+"F9.opExtrude","SWEPT_FACE",FACE,{"disambiguationData":[OSD([sQuery(id+"F8.wireOp",EDGE,"E68")])]})]});
            var Q14;
            Q14=makeQuery(id+"F10.opExtrude","CAP_EDGE",EDGE,{"disambiguationData":[OSD([sQuery(id+"F7.wireOp",EDGE,"E47.top")])],"isStart":false});
            var Q15;
            Q15=makeQuery(id+"F10.boolean.opBoolean","MERGE",EDGE,{"derivedFrom":[makeQuery(id+"F10.opExtrude","CAP_EDGE",EDGE,{"disambiguationData":[OSD([sQuery(id+"F1.wireOp",EDGE,"E6"),sQuery(id+"F1.wireOp",EDGE,"E7"),sQuery(id+"F1.wireOp",EDGE,"E13")])],"isStart":false}),makeQuery(id+"F10.opExtrude","CAP_EDGE",EDGE,{"disambiguationData":[OSD([sQuery(id+"F7.wireOp",EDGE,"E48.top")])],"isStart":false})]});
            var Q16;
            Q16=makeQuery(id+"F10.opExtrude","CAP_EDGE",EDGE,{"disambiguationData":[OSD([sQuery(id+"F7.wireOp",EDGE,"E47.right")])],"isStart":false});
            var Q17;
            Q17=makeQuery(id+"F10.opExtrude","CAP_EDGE",EDGE,{"disambiguationData":[OSD([sQuery(id+"F7.wireOp",EDGE,"E48.right")])],"isStart":false});
            fillet(context, id + "F14", {"entities" : qUnion([Q0, Q1, Q2, Q3, Q4, Q5, Q6, Q7, Q8, Q9, Q10, Q11, Q12, Q13, Q14, Q15, Q16, Q17]), "radius" : 4 * mm, "tangentPropagation" : true, "allowEdgeOverflow" : false});
        }
        {
            var Q0;
            {var subQ4=sQuery(id+"F1.wireOp",EDGE,"E12");var subQ5=sQuery(id+"F1.wireOp",EDGE,"E11");Q0=makeQuery(id+"FcCoG44jGWUjaJj_4.boolean.opBoolean","SPLIT",FACE,{"disambiguationData":[TD([makeQuery(id+"F2.opExtrude","SWEPT_FACE",FACE,{"disambiguationData":[OSD([subQ5])]})])],"derivedFrom":makeQuery(id+"F2.opExtrude","SWEPT_FACE",FACE,{"disambiguationData":[OSD([subQ4])]})});}
            var sketch = newSketch(context, id + "F15", { "sketchPlane" : qUnion([Q0])});
            skLineSegment(sketch, "E77.bottom", {"start": v(-33.02, 34.06) * mm, "end": v(33.02, 34.06) * mm});
            skLineSegment(sketch, "E77.top", {"start": v(-33.02, -35.94) * mm, "end": v(33.02, -35.94) * mm});
            skLineSegment(sketch, "E77.left", {"start": v(-33.02, 34.06) * mm, "end": v(-33.02, -35.94) * mm});
            skLineSegment(sketch, "E77.right", {"start": v(33.02, 34.06) * mm, "end": v(33.02, -35.94) * mm});
            skSolve(sketch);
        }
        {
            var Q0;
            Q0 = qSketchRegion(id + "F15", true);
            var Q1;
            Q1=makeQuery(id+"F2.opExtrude","SWEPT_FACE",FACE,{"disambiguationData":[OSD([sQuery(id+"F1.wireOp",EDGE,"E7")])]});
            extrude(context, id + "F16", {"entities" : qUnion([Q0]), "operationType" : NewBodyOperationType.REMOVE, "endBound" : BoundingType.UP_TO_SURFACE, "oppositeDirection" : true, "endBoundEntityFace" : qUnion([Q1]), "depth" : 25 * mm});
        }
        {
            var Q0;
            {var subQ2=sQuery(id+"F1.wireOp",EDGE,"E7");Q0=makeQuery(id+"F4.boolean.opBoolean","SPLIT",FACE,{"disambiguationData":[TD([makeQuery(id+"F4.opExtrude","SWEPT_FACE",FACE,{"disambiguationData":[OSD([sQuery(id+"F0.wireOp",EDGE,"E1")])]})])],"derivedFrom":makeQuery(id+"FAsxnAHrsa3fCM4_1.opExtrude","SWEPT_FACE",FACE,{"disambiguationData":[OSD([subQ2])]})});}
            var Q1;
            {var subQ2=sQuery(id+"F1.wireOp",EDGE,"E7");Q1=makeQuery(id+"F4.boolean.opBoolean","SPLIT",FACE,{"disambiguationData":[TD([makeQuery(id+"F4.opExtrude","SWEPT_FACE",FACE,{"disambiguationData":[OSD([sQuery(id+"F0.wireOp",EDGE,"E2")])]})])],"derivedFrom":makeQuery(id+"FAsxnAHrsa3fCM4_1.opExtrude","SWEPT_FACE",FACE,{"disambiguationData":[OSD([subQ2])]})});}
            var Q2;
            {var subQ2=sQuery(id+"F1.wireOp",EDGE,"amrAWSQz-qLGa-weJD-g3JT-vMCCPkI0vDQE");Q2=makeQuery(id+"F4.boolean.opBoolean","SPLIT",FACE,{"disambiguationData":[TD([makeQuery(id+"F4.opExtrude","SWEPT_FACE",FACE,{"disambiguationData":[OSD([sQuery(id+"F0.wireOp",EDGE,"E2")])]})])],"derivedFrom":makeQuery(id+"FAsxnAHrsa3fCM4_1.opExtrude","SWEPT_FACE",FACE,{"disambiguationData":[OSD([subQ2])]})});}
            var Q3;
            {var subQ2=sQuery(id+"F1.wireOp",EDGE,"amrAWSQz-qLGa-weJD-g3JT-vMCCPkI0vDQE");Q3=makeQuery(id+"F4.boolean.opBoolean","SPLIT",FACE,{"disambiguationData":[TD([makeQuery(id+"F4.opExtrude","SWEPT_FACE",FACE,{"disambiguationData":[OSD([sQuery(id+"F0.wireOp",EDGE,"E1")])]})])],"derivedFrom":makeQuery(id+"FAsxnAHrsa3fCM4_1.opExtrude","SWEPT_FACE",FACE,{"disambiguationData":[OSD([subQ2])]})});}
            var Q4;
            Q4=makeQuery(id+"F3.opExtrude","SWEPT_BODY",BODY,{"disambiguationData":[OSD([sQuery(id+"F1.wireOp",EDGE,"E6"),sQuery(id+"F1.wireOp",EDGE,"E7"),sQuery(id+"F1.wireOp",EDGE,"E9"),sQuery(id+"F1.wireOp",EDGE,"E14")])]});
            var Q5;
            Q5=makeQuery(id+"F2.opExtrude","SWEPT_BODY",BODY,{"disambiguationData":[OSD([sQuery(id+"F1.wireOp",EDGE,"E7"),sQuery(id+"F1.wireOp",EDGE,"E9"),sQuery(id+"F1.wireOp",EDGE,"E11"),sQuery(id+"F1.wireOp",EDGE,"E12"),sQuery(id+"F1.wireOp",EDGE,"E13"),sQuery(id+"F1.wireOp",EDGE,"E15")])]});
            shell(context, id + "F17", {"isHollow" : true, "entities" : qUnion([Q0, Q1, Q2, Q3]), "parts" : qUnion([Q4, Q5]), "thickness" : 1.2 * mm, "oppositeDirection" : true});
        }
    });
